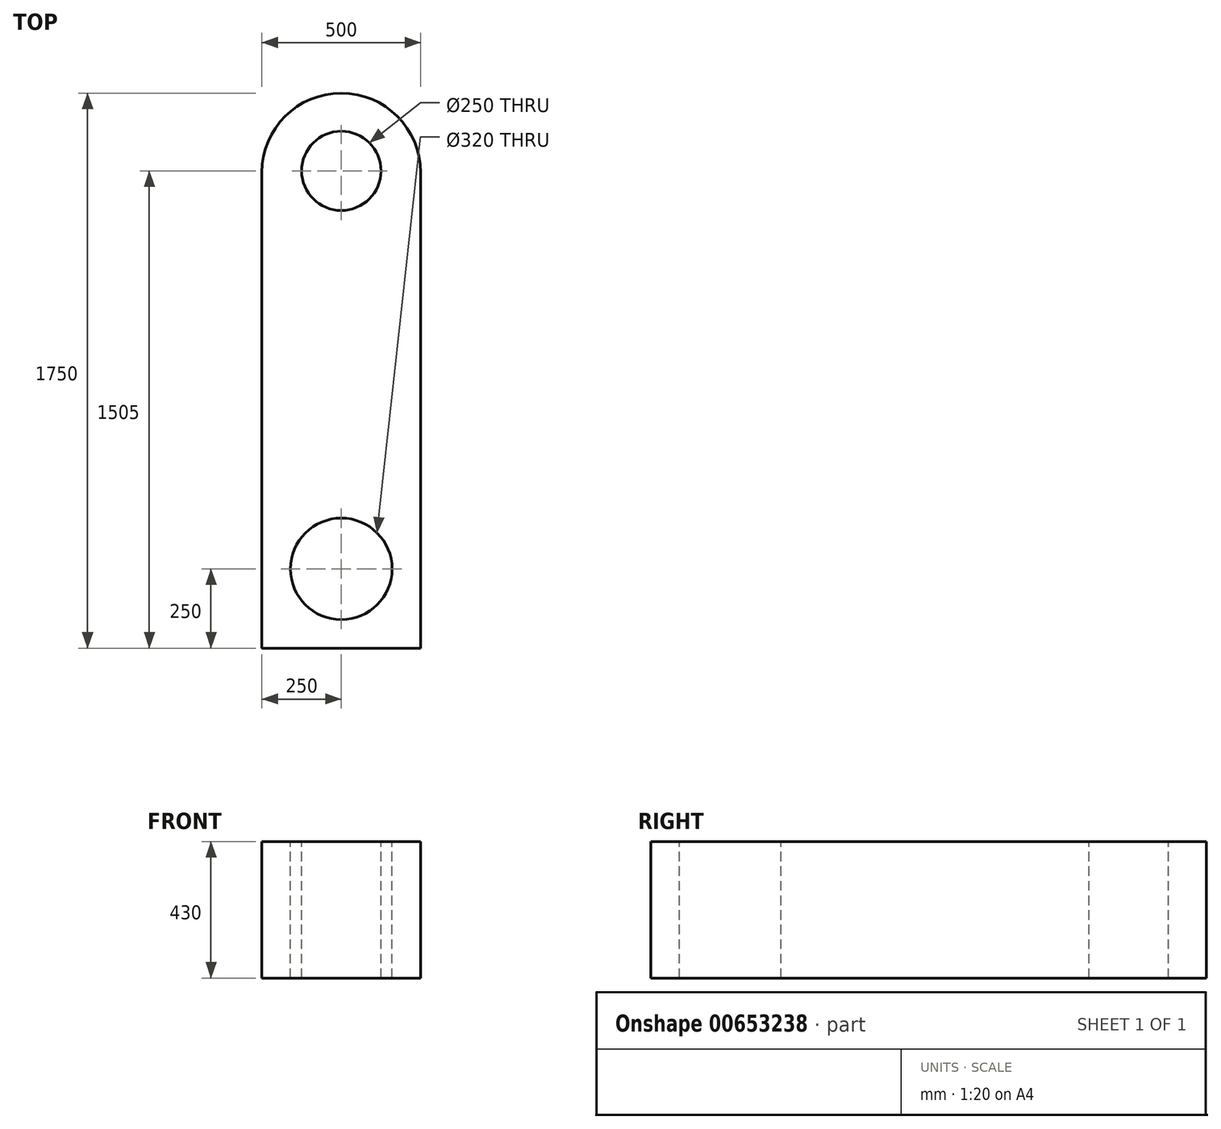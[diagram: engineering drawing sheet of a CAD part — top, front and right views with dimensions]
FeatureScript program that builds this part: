
annotation { "Feature Type Name" : "Feature", "Feature Type Description" : "" }
export const myFeature = defineFeature(function(context is Context, id is Id, definition is map)
    precondition{}
    {
        {
            var Q0;
            Q0=qCreatedBy(makeId("Front.planeOp"),FACE);
            var sketch = newSketch(context, id + "F0", { "sketchPlane" : qUnion([Q0])});
            skLineSegment(sketch, "E0.bottom", {"start": v(250, 215) * mm, "end": v(-250, 215) * mm});
            skLineSegment(sketch, "E0.top", {"start": v(250, -215) * mm, "end": v(-250, -215) * mm});
            skLineSegment(sketch, "E0.left", {"start": v(250, 215) * mm, "end": v(250, -215) * mm});
            skLineSegment(sketch, "E0.right", {"start": v(-250, 215) * mm, "end": v(-250, -215) * mm});
            skPoint(sketch, "E0.middle", {"position": v(0, 0) * mm});
            skSolve(sketch);
        }
        {
            var Q0;
            Q0 = qSketchRegion(id + "F0", true);
            extrude(context, id + "F1", {"entities" : qUnion([Q0]), "oppositeDirection" : true, "depth" : 1500 * mm, "offsetDistance" : 25 * mm});
        }
        {
            var Q0;
            Q0=makeQuery(id+"F1.opExtrude","SWEPT_FACE",FACE,{"disambiguationData":[OSD([sQuery(id+"F0.wireOp",EDGE,"E0.bottom")])]});
            var sketch = newSketch(context, id + "F2", { "sketchPlane" : qUnion([Q0])});
            skArc(sketch, "E1", {"start": v(250, 1500) * mm, "mid": v(0, 1750) * mm, "end": v(-250, 1500) * mm});
            skLineSegment(sketch, "E2", {"start": v(-250, 1500) * mm, "end": v(250, 1500) * mm});
            skSolve(sketch);
        }
        {
            var Q0;
            Q0 = qSketchRegion(id + "F2", true);
            extrude(context, id + "F3", {"entities" : qUnion([Q0]), "operationType" : NewBodyOperationType.ADD, "oppositeDirection" : true, "depth" : 430 * mm, "offsetDistance" : 25 * mm});
        }
        {
            var Q0;
            Q0=makeQuery(id+"F3.boolean.opBoolean","MERGE",FACE,{"derivedFrom":[makeQuery(id+"F1.opExtrude","SWEPT_FACE",FACE,{"disambiguationData":[OSD([sQuery(id+"F0.wireOp",EDGE,"E0.bottom")])]}),makeQuery(id+"F3.opExtrude","CAP_FACE",FACE,{"disambiguationData":[OSD([sQuery(id+"F2.wireOp",EDGE,"E1"),sQuery(id+"F2.wireOp",EDGE,"E2")])],"isStart":true})]});
            var sketch = newSketch(context, id + "F4", { "sketchPlane" : qUnion([Q0])});
            skCircle(sketch, "E3", {"center": v(0, 1505) * mm, "radius": 125 * mm});
            skSolve(sketch);
        }
        {
            var Q0;
            Q0 = qSketchRegion(id + "F4", true);
            extrude(context, id + "F5", {"entities" : qUnion([Q0]), "operationType" : NewBodyOperationType.REMOVE, "oppositeDirection" : true, "depth" : 500 * mm, "offsetDistance" : 25 * mm});
        }
        {
            var Q0;
            Q0=makeQuery(id+"F3.boolean.opBoolean","MERGE",FACE,{"derivedFrom":[makeQuery(id+"F1.opExtrude","SWEPT_FACE",FACE,{"disambiguationData":[OSD([sQuery(id+"F0.wireOp",EDGE,"E0.bottom")])]}),makeQuery(id+"F3.opExtrude","CAP_FACE",FACE,{"disambiguationData":[OSD([sQuery(id+"F2.wireOp",EDGE,"E1"),sQuery(id+"F2.wireOp",EDGE,"E2")])],"isStart":true})]});
            var sketch = newSketch(context, id + "F6", { "sketchPlane" : qUnion([Q0])});
            skCircle(sketch, "E4", {"center": v(0, 250) * mm, "radius": 160 * mm});
            skSolve(sketch);
        }
        {
            var Q0;
            Q0 = qSketchRegion(id + "F6", true);
            extrude(context, id + "F7", {"entities" : qUnion([Q0]), "operationType" : NewBodyOperationType.REMOVE, "oppositeDirection" : true, "depth" : 500 * mm, "offsetDistance" : 25 * mm});
        }
    });
